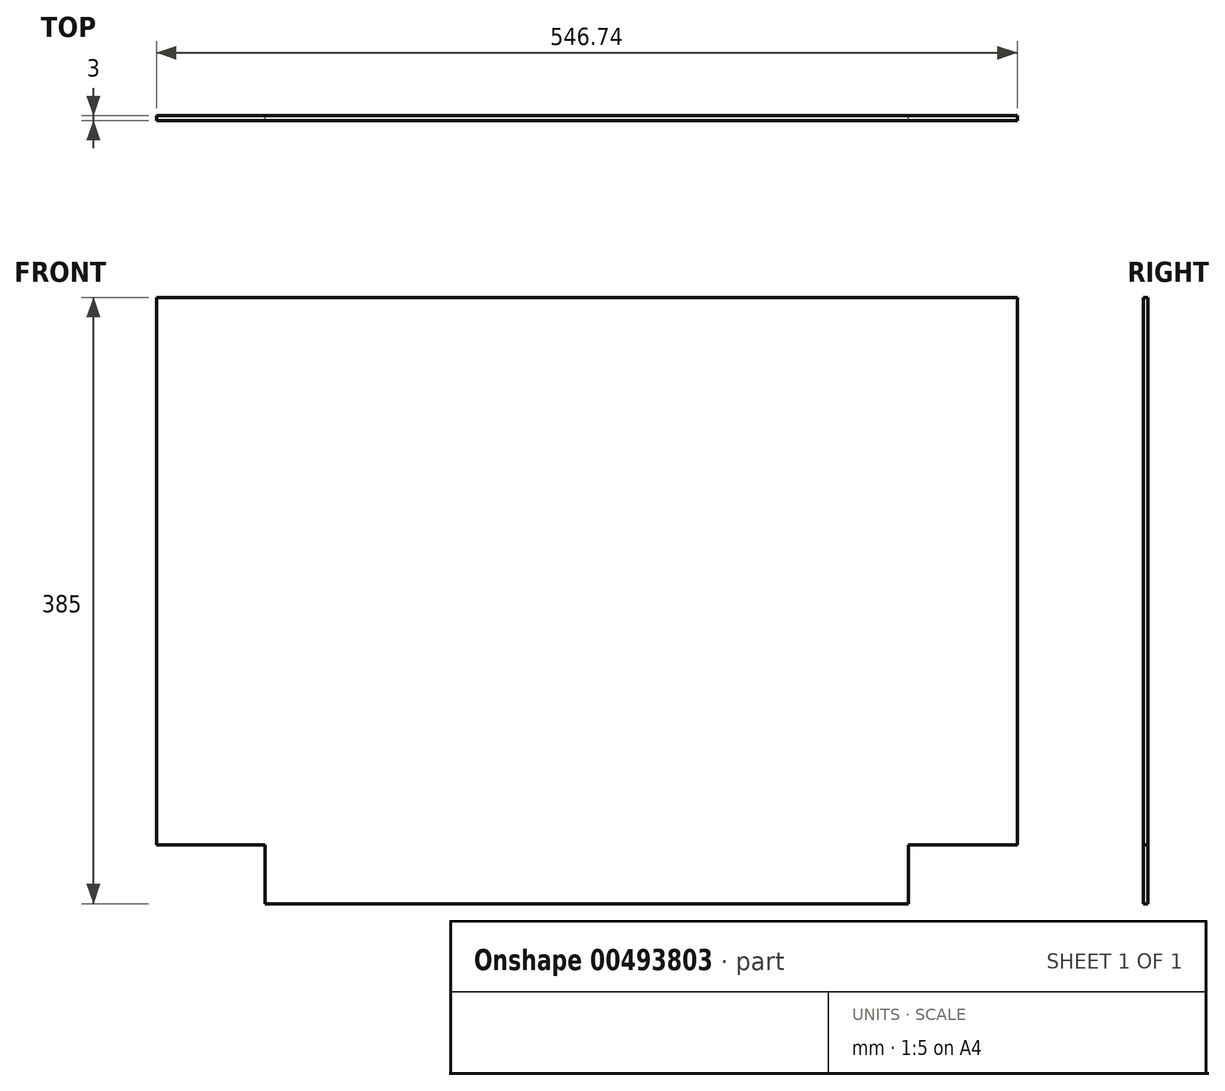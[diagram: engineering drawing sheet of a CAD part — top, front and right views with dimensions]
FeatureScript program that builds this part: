
annotation { "Feature Type Name" : "Feature", "Feature Type Description" : "" }
export const myFeature = defineFeature(function(context is Context, id is Id, definition is map)
    precondition{}
    {
        {
            var Q0;
            Q0=qCreatedBy(makeId("Front.planeOp"),FACE);
            var sketch = newSketch(context, id + "F0", { "sketchPlane" : qUnion([Q0])});
            skLineSegment(sketch, "E0.bottom", {"start": v(273.37, 173.75) * mm, "end": v(-273.37, 173.75) * mm});
            skLineSegment(sketch, "E0.top", {"start": v(273.37, -173.75) * mm, "end": v(-273.37, -173.75) * mm});
            skLineSegment(sketch, "E0.left", {"start": v(273.37, 173.75) * mm, "end": v(273.37, -173.75) * mm});
            skLineSegment(sketch, "E0.right", {"start": v(-273.37, 173.75) * mm, "end": v(-273.37, -173.75) * mm});
            skPoint(sketch, "E0.middle", {"position": v(0, 0) * mm});
            skSolve(sketch);
        }
        {
            var Q0;
            Q0=makeQuery(id+"F0.imprint","IMPRINT",FACE,{"disambiguationData":[TD([[makeQuery(id+"F0.imprint","IMPRINT",EDGE,{"derivedFrom":sQuery(id+"F0.wireOp",EDGE,"E0.bottom")}),1.0]])]});
            extrude(context, id + "F1", {"entities" : qUnion([Q0]), "depth" : 3 * mm});
        }
        {
            var Q0;
            Q0=makeQuery(id+"F1.opExtrude","SWEPT_FACE",FACE,{"disambiguationData":[OSD([sQuery(id+"F0.wireOp",EDGE,"E0.top")])]});
            var sketch = newSketch(context, id + "F2", { "sketchPlane" : qUnion([Q0])});
            skLineSegment(sketch, "E1", {"start": v(-273.37, 3) * mm, "end": v(-204.37, 3) * mm, "construction": true});
            skLineSegment(sketch, "E2", {"start": v(273.37, 3) * mm, "end": v(204.37, 3) * mm, "construction": true});
            skLineSegment(sketch, "E3.bottom", {"start": v(-204.37, 3) * mm, "end": v(204.37, 3) * mm});
            skLineSegment(sketch, "E3.top", {"start": v(-204.37, 0) * mm, "end": v(204.37, 0) * mm});
            skLineSegment(sketch, "E3.left", {"start": v(-204.37, 3) * mm, "end": v(-204.37, 0) * mm});
            skLineSegment(sketch, "E3.right", {"start": v(204.37, 3) * mm, "end": v(204.37, 0) * mm});
            skSolve(sketch);
        }
        {
            var Q0;
            Q0=makeQuery(id+"F2.imprint","IMPRINT",FACE,{"disambiguationData":[TD([[makeQuery(id+"F2.imprint","IMPRINT",EDGE,{"derivedFrom":sQuery(id+"F2.wireOp",EDGE,"E3.bottom")}),1.0]])]});
            extrude(context, id + "F3", {"entities" : qUnion([Q0]), "operationType" : NewBodyOperationType.ADD, "depth" : 37.5 * mm});
        }
    });
